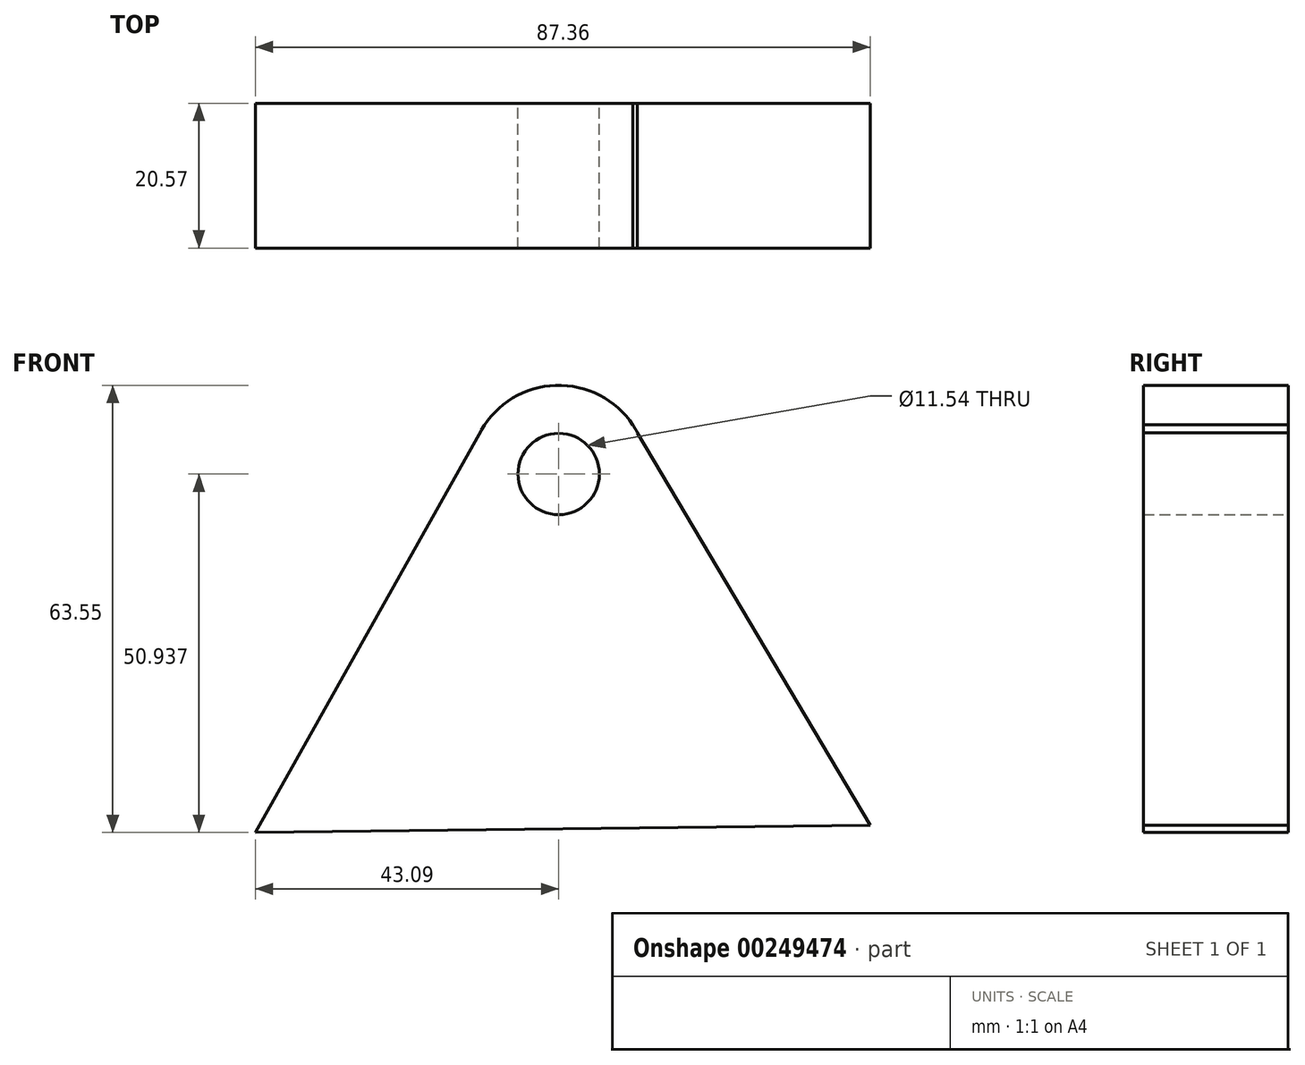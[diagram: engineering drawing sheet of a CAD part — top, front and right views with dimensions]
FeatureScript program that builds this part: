
annotation { "Feature Type Name" : "Feature", "Feature Type Description" : "" }
export const myFeature = defineFeature(function(context is Context, id is Id, definition is map)
    precondition{}
    {
        {
            var Q0;
            Q0=qCreatedBy(makeId("Front.planeOp"),FACE);
            var sketch = newSketch(context, id + "F0", { "sketchPlane" : qUnion([Q0])});
            skCircle(sketch, "E0.cCircle", {"center": v(0, 0) * mm, "radius": 50.44 * mm, "construction": true});
            skLineSegment(sketch, "E0.0", {"start": v(10.23, 32.2) * mm, "end": v(43.98, -24.7) * mm});
            skLineSegment(sketch, "E0.1", {"start": v(43.98, -24.7) * mm, "end": v(-43.38, -25.74) * mm});
            skLineSegment(sketch, "E0.2", {"start": v(-43.38, -25.74) * mm, "end": v(-11.3, 31.4) * mm});
            skArc(sketch, "E1", {"start": v(10.9, 31.07) * mm, "mid": v(10.57, 31.64) * mm, "end": v(10.23, 32.2) * mm});
            skArc(sketch, "E2.trimOffspring", {"start": v(-11.3, 31.4) * mm, "mid": v(-11.3, 31.38) * mm, "end": v(-11.32, 31.36) * mm});
            skArc(sketch, "E3", {"start": v(10.9, 31.07) * mm, "mid": v(-0.1, 37.8) * mm, "end": v(-11.3, 31.4) * mm});
            skSolve(sketch);
        }
        {
            var Q0;
            Q0 = qSketchRegion(id + "F0", true);
            extrude(context, id + "F1", {"entities" : qUnion([Q0]), "oppositeDirection" : true, "depth" : 20.57 * mm});
        }
        {
            var Q0;
            Q0=makeQuery(id+"F1.opExtrude","CAP_FACE",FACE,{"disambiguationData":[OSD([sQuery(id+"F0.wireOp",EDGE,"E0.0"),sQuery(id+"F0.wireOp",EDGE,"E0.1"),sQuery(id+"F0.wireOp",EDGE,"E0.2"),sQuery(id+"F0.wireOp",EDGE,"E1"),sQuery(id+"F0.wireOp",EDGE,"E2.trimOffspring"),sQuery(id+"F0.wireOp",EDGE,"E3")])],"isStart":false});
            var sketch = newSketch(context, id + "F2", { "sketchPlane" : qUnion([Q0])});
            skPoint(sketch, "E4", {"position": v(0.3, 25.2) * mm});
            skCircle(sketch, "E5", {"center": v(0.3, 25.2) * mm, "radius": 5.77 * mm});
            skSolve(sketch);
        }
        {
            var Q0;
            Q0=makeQuery(id+"F2.imprint","IMPRINT",FACE,{"disambiguationData":[TD([[makeQuery(id+"F2.imprint","IMPRINT",EDGE,{"derivedFrom":sQuery(id+"F2.wireOp",EDGE,"E5")}),1.0]])]});
            extrude(context, id + "F3", {"entities" : qUnion([Q0]), "operationType" : NewBodyOperationType.REMOVE, "oppositeDirection" : true, "depth" : 25.4 * mm});
        }
    });
